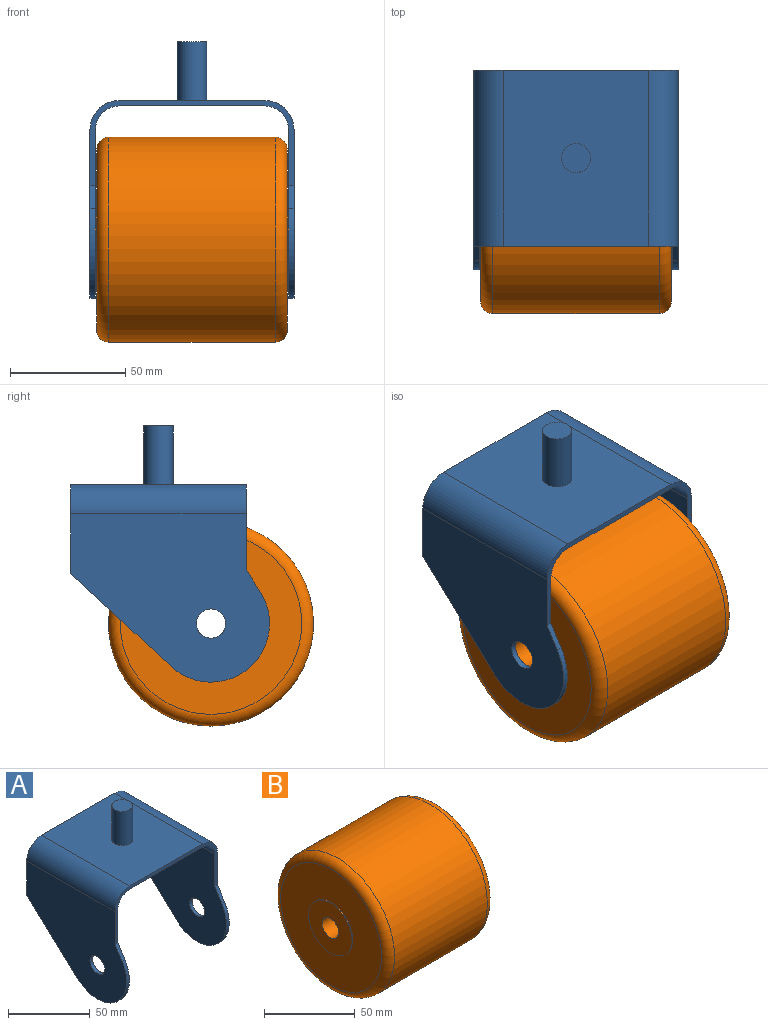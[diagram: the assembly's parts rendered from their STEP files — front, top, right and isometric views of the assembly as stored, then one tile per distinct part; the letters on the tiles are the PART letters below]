
ASSEMBLY  parts=2 mates=1
PART A: 22 faces, bbox 88.5x86.3x111.1 mm
  f0: plane 86.31x73.03mm, normal (-1,0,0), area 4493.5mm2, adj f3,f6,f7,f8,f9,f10,f11
  f1: plane 86.31x73.03mm, normal (1,0,0), area 4493.5mm2, adj f4,f6,f7,f8,f9,f10,f11
  f2: plane 76.2x63.11mm, normal (0,0,1), area 4682mm2, adj f4,f6,f9,f15,f20
  f3: cylinder r=10.34mm len=76.2mm, axis (0,1,0), area 1237.4mm2, adj f0,f5,f6,f9
  f4: cylinder r=12.7mm len=76.2mm, axis (0,1,0), area 1520.1mm2, adj f1,f2,f6,f9
  f5: plane 76.2x63.11mm, normal (0,0,-1), area 4808.7mm2, adj f3,f6,f9,f14
  f6: plane 88.51x36.95mm, normal (0,-1,0), area 349.1mm2, adj f0,f1,f2,f3,f4,f5,f8,f12
  f7: cylinder r=25.4mm len=42.65mm, axis (-1,0,0), area 172.8mm2, adj f0,f1,f8,f10
  f8: plane 9.83x6.2mm, normal (0,-0.85,0.53), area 27.4mm2, adj f0,f1,f6,f7
  f9: plane 88.51x38.59mm, normal (0,1,0), area 356.9mm2, adj f0,f1,f2,f3,f4,f5,f10,f12
  f10: plane 43.66x40.38mm, normal (0,0.68,-0.73), area 140.5mm2, adj f0,f1,f7,f9
  f11: cylinder r=6.35mm len=12.7mm, axis (-1,0,0), area 94.2mm2, adj f0,f1
  f12: plane 86.31x73.03mm, normal (1,0,0), area 4493.5mm2, adj f6,f9,f14,f16,f17,f18,f19
  f13: plane 86.31x73.03mm, normal (-1,0,0), area 4493.5mm2, adj f6,f9,f15,f16,f17,f18,f19
  f14: cylinder r=10.34mm len=76.2mm, axis (0,1,0), area 1237.4mm2, adj f5,f6,f9,f12
  f15: cylinder r=12.7mm len=76.2mm, axis (0,1,0), area 1520.1mm2, adj f2,f6,f9,f13
  f16: cylinder r=25.4mm len=42.65mm, axis (1,0,0), area 172.8mm2, adj f12,f13,f17,f18
  f17: plane 9.83x6.2mm, normal (0,-0.85,0.53), area 27.4mm2, adj f6,f12,f13,f16
  f18: plane 43.66x40.38mm, normal (0,0.68,-0.73), area 140.5mm2, adj f9,f12,f13,f16
  f19: cylinder r=6.35mm len=12.7mm, axis (1,0,0), area 94.2mm2, adj f12,f13
  f20: cylinder r=6.35mm len=25.4mm, axis (0,0,-1), area 1013.4mm2, adj f2,f21
  f21: plane 12.7x12.7mm, normal (0,0,1), area 126.7mm2, adj f20
PART B: 10 faces, bbox 83.7x96.2x96.2 mm
  f0: cylinder r=44.45mm len=88.9mm, axis (-1,0,0), area 20217.6mm2, adj f5,f9
  f1: plane 78.74x78.74mm, normal (1,0,0), area 3968.6mm2, adj f2,f5
  f2: cylinder r=16.93mm len=33.87mm, axis (-1,0,0), area 62.8mm2, adj f1,f3
  f3: plane 33.87x33.87mm, normal (1,0,0), area 774.1mm2, adj f2,f4
  f4: cylinder r=6.35mm len=83.73mm, axis (-1,0,0), area 3340.7mm2, adj f3,f8
  f5: torus R=39.37mm, axis (1,0,0), area 2136.1mm2, adj f0,f1
  f6: plane 78.74x78.74mm, normal (-1,0,0), area 3968.6mm2, adj f7,f9
  f7: cylinder r=16.93mm len=33.87mm, axis (1,0,0), area 62.8mm2, adj f6,f8
  f8: plane 33.87x33.87mm, normal (-1,0,0), area 774.1mm2, adj f4,f7
  f9: torus R=39.37mm, axis (-1,0,0), area 2136.1mm2, adj f0,f6
PLACE A at identity fixed
PLACE B at identity
MATE revolute B.f0 <-> A.f7  axis (-1,0,0) through (0,0,44.45)mm
